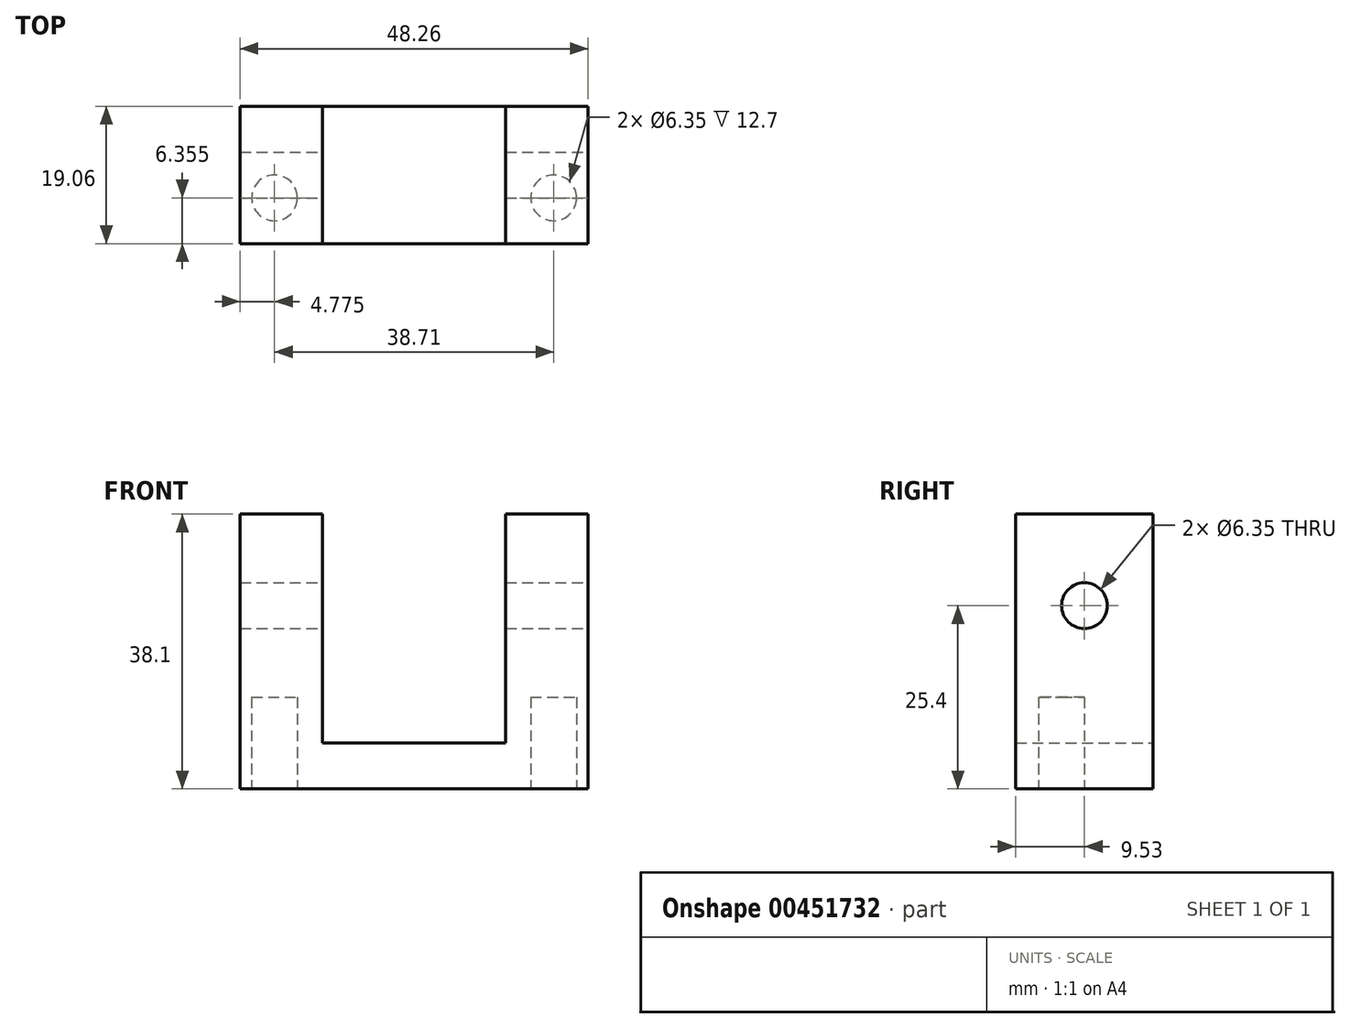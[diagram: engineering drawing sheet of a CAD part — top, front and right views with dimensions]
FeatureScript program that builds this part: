
annotation { "Feature Type Name" : "Feature", "Feature Type Description" : "" }
export const myFeature = defineFeature(function(context is Context, id is Id, definition is map)
    precondition{}
    {
        {
            var Q0;
            Q0=qCreatedBy(makeId("Front.planeOp"),FACE);
            var sketch = newSketch(context, id + "F0", { "sketchPlane" : qUnion([Q0])});
            skLineSegment(sketch, "E0", {"start": v(0, 0) * mm, "end": v(-24.13, 0) * mm});
            skLineSegment(sketch, "E1", {"start": v(-24.13, 0) * mm, "end": v(-24.13, 38.1) * mm});
            skLineSegment(sketch, "E2", {"start": v(-24.13, 38.1) * mm, "end": v(-12.7, 38.1) * mm});
            skLineSegment(sketch, "E3", {"start": v(-12.7, 38.1) * mm, "end": v(-12.7, 6.35) * mm});
            skLineSegment(sketch, "E4", {"start": v(-12.7, 6.35) * mm, "end": v(0, 6.35) * mm});
            skLineSegment(sketch, "E5.MirrorCS", {"start": v(24.13, 0) * mm, "end": v(24.13, 38.1) * mm});
            skLineSegment(sketch, "E6.MirrorCS", {"start": v(0, 0) * mm, "end": v(24.13, 0) * mm});
            skLineSegment(sketch, "E7.MirrorCS", {"start": v(12.7, 6.35) * mm, "end": v(0, 6.35) * mm});
            skLineSegment(sketch, "E8.MirrorCS", {"start": v(12.7, 38.1) * mm, "end": v(12.7, 6.35) * mm});
            skLineSegment(sketch, "E9.MirrorCS", {"start": v(24.13, 38.1) * mm, "end": v(12.7, 38.1) * mm});
            skSolve(sketch);
        }
        {
            var Q0;
            Q0 = qSketchRegion(id + "F0", true);
            extrude(context, id + "F1", {"entities" : qUnion([Q0]), "endBound" : BoundingType.SYMMETRIC, "depth" : 19.05 * mm});
        }
        {
            var Q0;
            Q0=makeQuery(id+"F1.opExtrude","SWEPT_FACE",FACE,{"disambiguationData":[OSD([sQuery(id+"F0.wireOp",EDGE,"E5.MirrorCS")])]});
            var sketch = newSketch(context, id + "F2", { "sketchPlane" : qUnion([Q0])});
            skCircle(sketch, "E10", {"center": v(0, 25.4) * mm, "radius": 3.18 * mm});
            skSolve(sketch);
        }
        {
            var Q0;
            Q0 = qSketchRegion(id + "F2", true);
            extrude(context, id + "F3", {"entities" : qUnion([Q0]), "operationType" : NewBodyOperationType.REMOVE, "oppositeDirection" : true, "depth" : 59.18 * mm});
        }
        {
            var Q0;
            Q0=makeQuery(id+"F1.opExtrude","SWEPT_FACE",FACE,{"disambiguationData":[OSD([sQuery(id+"F0.wireOp",EDGE,"E0"),sQuery(id+"F0.wireOp",EDGE,"E6.MirrorCS")])]});
            var sketch = newSketch(context, id + "F4", { "sketchPlane" : qUnion([Q0])});
            skCircle(sketch, "E11", {"center": v(-19.35, 3.17) * mm, "radius": 3.18 * mm});
            skCircle(sketch, "E12.MirrorC", {"center": v(19.35, 3.17) * mm, "radius": 3.18 * mm});
            skSolve(sketch);
        }
        {
            var Q0;
            Q0 = qSketchRegion(id + "F4", true);
            extrude(context, id + "F5", {"entities" : qUnion([Q0]), "operationType" : NewBodyOperationType.REMOVE, "oppositeDirection" : true, "depth" : 12.7 * mm});
        }
    });
